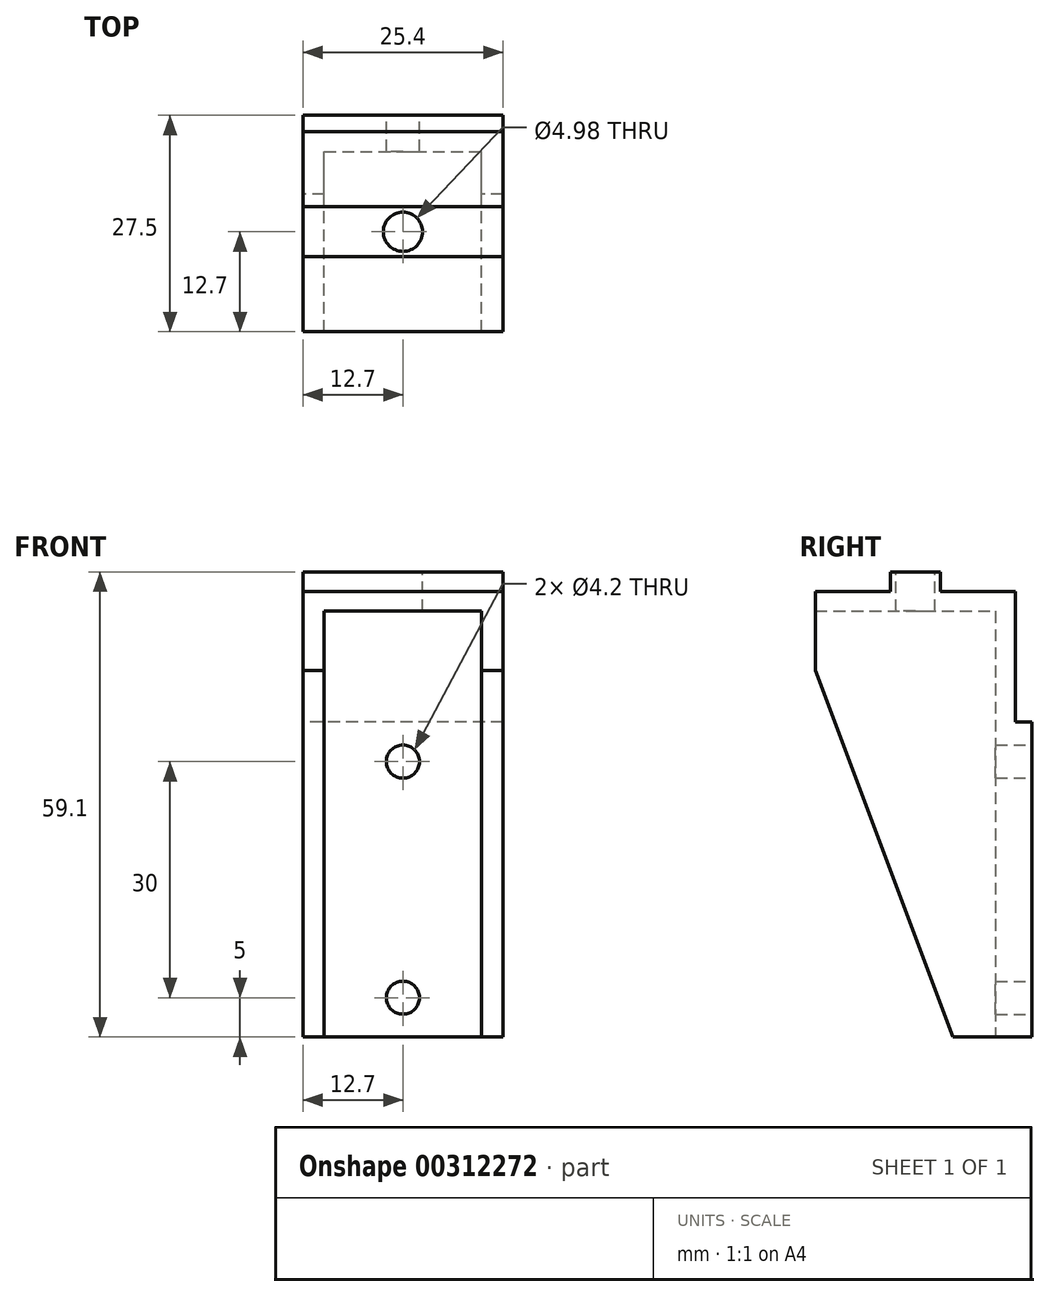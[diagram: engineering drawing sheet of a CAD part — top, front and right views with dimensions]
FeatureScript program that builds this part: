
annotation { "Feature Type Name" : "Feature", "Feature Type Description" : "" }
export const myFeature = defineFeature(function(context is Context, id is Id, definition is map)
    precondition{}
    {
        {
            var Q0;
            Q0=qCreatedBy(makeId("Right.planeOp"),FACE);
            var sketch = newSketch(context, id + "F0", { "sketchPlane" : qUnion([Q0])});
            skLineSegment(sketch, "E0", {"start": v(0, 0) * mm, "end": v(0, 40) * mm});
            skLineSegment(sketch, "E1", {"start": v(0, 40) * mm, "end": v(-2.1, 40) * mm});
            skLineSegment(sketch, "E2", {"start": v(-2.1, 40) * mm, "end": v(-2.1, 56.6) * mm});
            skLineSegment(sketch, "E3", {"start": v(-2.1, 56.6) * mm, "end": v(-27.5, 56.6) * mm});
            skLineSegment(sketch, "E4", {"start": v(-27.5, 56.6) * mm, "end": v(-27.5, 46.6) * mm});
            skLineSegment(sketch, "E5", {"start": v(-27.5, 46.6) * mm, "end": v(-10, 0) * mm});
            skLineSegment(sketch, "E6", {"start": v(-10, 0) * mm, "end": v(0, 0) * mm});
            skPoint(sketch, "E7", {"position": v(0, 35) * mm});
            skPoint(sketch, "E8", {"position": v(0, 5) * mm});
            skLineSegment(sketch, "E9", {"start": v(-27.5, 54.1) * mm, "end": v(-4.6, 54.1) * mm});
            skLineSegment(sketch, "E10", {"start": v(-4.6, 54.1) * mm, "end": v(-4.6, 0) * mm});
            skSolve(sketch);
        }
        {
            var Q0;
            {var subQ2=sQuery(id+"F0.wireOp",EDGE,"E5");Q0=makeQuery(id+"F0.imprint","IMPRINT",FACE,{"disambiguationData":[TD([[makeQuery(id+"F0.imprint","IMPRINT",EDGE,{"derivedFrom":subQ2}),1.0]])]});}
            var Q1;
            {var subQ1=sQuery(id+"F0.wireOp",EDGE,"E0");Q1=makeQuery(id+"F0.imprint","IMPRINT",FACE,{"disambiguationData":[TD([[makeQuery(id+"F0.imprint","IMPRINT",EDGE,{"derivedFrom":subQ1}),1.0]])]});}
            extrude(context, id + "F1", {"entities" : qUnion([Q0, Q1]), "endBound" : BoundingType.SYMMETRIC, "depth" : 25.4 * mm});
        }
        {
            var Q0;
            {var subQ2=sQuery(id+"F0.wireOp",EDGE,"E5");Q0=makeQuery(id+"F0.imprint","IMPRINT",FACE,{"disambiguationData":[TD([[makeQuery(id+"F0.imprint","IMPRINT",EDGE,{"derivedFrom":subQ2}),1.0]])]});}
            extrude(context, id + "F2", {"entities" : qUnion([Q0]), "operationType" : NewBodyOperationType.REMOVE, "endBound" : BoundingType.SYMMETRIC, "oppositeDirection" : true, "depth" : 20 * mm});
        }
        {
            var Q0;
            Q0=makeQuery(id+"F1.opExtrude","SWEPT_FACE",FACE,{"disambiguationData":[OSD([sQuery(id+"F0.wireOp",EDGE,"E0")])]});
            var sketch = newSketch(context, id + "F3", { "sketchPlane" : qUnion([Q0])});
            skPoint(sketch, "E11.0", {"position": v(0, 35) * mm});
            skPoint(sketch, "E11.1", {"position": v(0, 5) * mm});
            skSolve(sketch);
        }
        {
            var Q0;
            Q0=sQuery(id+"F3.wireOp",VERTEX,"E11.0");
            var Q1;
            Q1=sQuery(id+"F3.wireOp",VERTEX,"E11.1");
            var Q2;
            Q2=makeQuery(id+"F1.opExtrude","SWEPT_BODY",BODY,{"disambiguationData":[OSD([sQuery(id+"F0.wireOp",EDGE,"E0"),sQuery(id+"F0.wireOp",EDGE,"E1"),sQuery(id+"F0.wireOp",EDGE,"E2"),sQuery(id+"F0.wireOp",EDGE,"E3"),sQuery(id+"F0.wireOp",EDGE,"E4"),sQuery(id+"F0.wireOp",EDGE,"E5"),sQuery(id+"F0.wireOp",EDGE,"E6")])]});
            hole(context, id + "F4", {"style" : HoleStyle.SIMPLE, "endStyle" : HoleEndStyle.THROUGH, "standardTappedOrClearance" : lookupTablePath({ "standard" : "ISO", "fit" : "Close", "size" : "M4", "type" : "Clearance" }), "standardBlindInLast" : lookupTablePath({ "fit" : "Close", "standard" : "ISO", "size" : "M4", "type" : "Clearance" }), "holeDiameter" : 4.2 * mm, "tappedDepth" : 12 * mm, "tapClearance" : 3, "locations" : qUnion([Q0, Q1]), "scope" : qUnion([Q2])});
        }
        {
            var Q0;
            Q0=makeQuery(id+"F1.opExtrude","SWEPT_FACE",FACE,{"disambiguationData":[OSD([sQuery(id+"F0.wireOp",EDGE,"E3")])]});
            var sketch = newSketch(context, id + "F5", { "sketchPlane" : qUnion([Q0])});
            skPoint(sketch, "E12", {"position": v(0, -14.8) * mm});
            skPoint(sketch, "E12.positionSnap0", {"position": v(-12.7, -14.8) * mm});
            skSolve(sketch);
        }
        {
            var Q0;
            Q0=sQuery(id+"F5.wireOp",VERTEX,"E12");
            var Q1;
            Q1=makeQuery(id+"F1.opExtrude","SWEPT_BODY",BODY,{"disambiguationData":[OSD([sQuery(id+"F0.wireOp",EDGE,"E0"),sQuery(id+"F0.wireOp",EDGE,"E1"),sQuery(id+"F0.wireOp",EDGE,"E2"),sQuery(id+"F0.wireOp",EDGE,"E3"),sQuery(id+"F0.wireOp",EDGE,"E4"),sQuery(id+"F0.wireOp",EDGE,"E5"),sQuery(id+"F0.wireOp",EDGE,"E6")])]});
            hole(context, id + "F6", {"style" : HoleStyle.SIMPLE, "endStyle" : HoleEndStyle.THROUGH, "standardTappedOrClearance" : lookupTablePath({ "standard" : "ANSI", "fit" : "Close", "size" : "#10", "type" : "Clearance" }), "standardBlindInLast" : lookupTablePath({ "fit" : "Close", "standard" : "ANSI", "size" : "#10", "type" : "Clearance" }), "holeDiameter" : 4.98 * mm, "tappedDepth" : 12 * mm, "tapClearance" : 3, "locations" : qUnion([Q0]), "scope" : qUnion([Q1])});
        }
        {
            var Q0;
            Q0=makeQuery(id+"F1.opExtrude","SWEPT_FACE",FACE,{"disambiguationData":[OSD([sQuery(id+"F0.wireOp",EDGE,"E3")])]});
            var sketch = newSketch(context, id + "F7", { "sketchPlane" : qUnion([Q0])});
            skLineSegment(sketch, "E13", {"start": v(-12.7, -11.63) * mm, "end": v(12.7, -11.63) * mm});
            skLineSegment(sketch, "E14", {"start": v(-12.7, -17.98) * mm, "end": v(12.7, -17.98) * mm});
            skLineSegment(sketch, "E15", {"start": v(12.7, -17.98) * mm, "end": v(12.7, -11.63) * mm});
            skLineSegment(sketch, "E16", {"start": v(-12.7, -11.63) * mm, "end": v(-12.7, -17.98) * mm});
            skLineSegment(sketch, "E17", {"start": v(-12.7, -14.8) * mm, "end": v(0, -14.8) * mm, "construction": true});
            skLineSegment(sketch, "E18", {"start": v(0, -14.8) * mm, "end": v(12.7, -14.8) * mm, "construction": true});
            skSolve(sketch);
        }
        {
            var Q0;
            Q0=makeQuery(id+"F7.imprint","IMPRINT",FACE,{"disambiguationData":[TD([[makeQuery(id+"F7.imprint","IMPRINT",EDGE,{"derivedFrom":sQuery(id+"F7.wireOp",EDGE,"E13")}),-1.0]])]});
            extrude(context, id + "F8", {"entities" : qUnion([Q0]), "operationType" : NewBodyOperationType.ADD, "depth" : 2.5 * mm});
        }
    });
